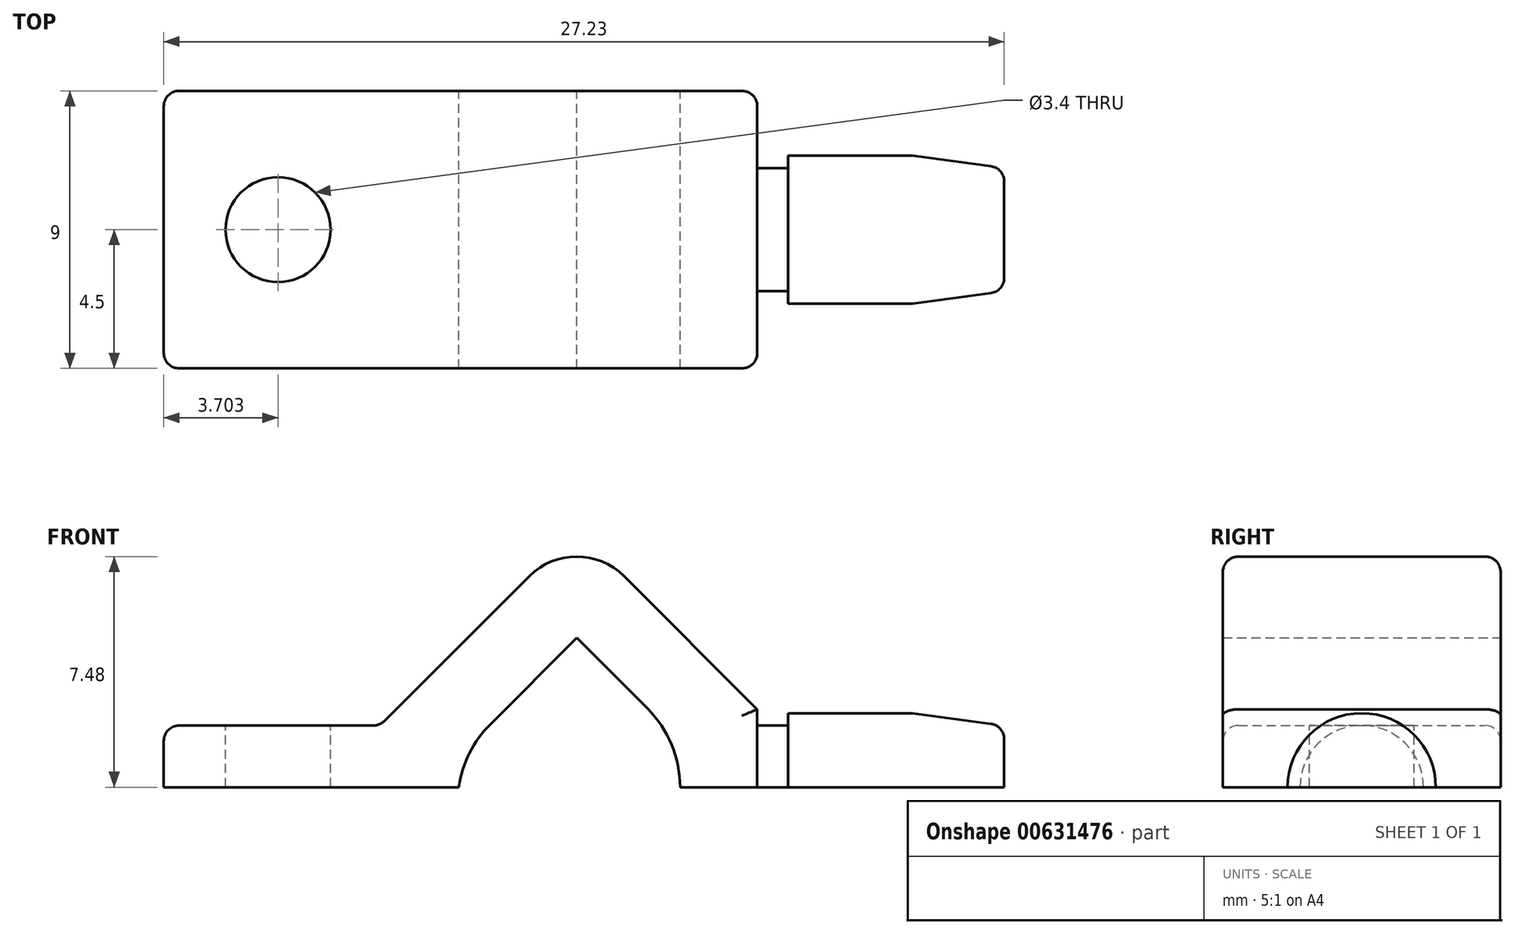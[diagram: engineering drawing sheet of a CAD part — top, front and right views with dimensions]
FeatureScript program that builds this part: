
annotation { "Feature Type Name" : "Feature", "Feature Type Description" : "" }
export const myFeature = defineFeature(function(context is Context, id is Id, definition is map)
    precondition{}
    {
        {
            var Q0;
            Q0=qCreatedBy(makeId("Front.planeOp"),FACE);
            var sketch = newSketch(context, id + "F0", { "sketchPlane" : qUnion([Q0])});
            skArc(sketch, "E0", {"start": v(-2.55, 2.05) * mm, "mid": v(-3.22, 1.1) * mm, "end": v(-3.57, 0) * mm});
            skLineSegment(sketch, "E1", {"start": v(0.25, 4.84) * mm, "end": v(2.55, 2.55) * mm});
            skLineSegment(sketch, "E2", {"start": v(0.25, 4.84) * mm, "end": v(-2.55, 2.05) * mm});
            skLineSegment(sketch, "E3", {"start": v(-13.13, 0) * mm, "end": v(-3.57, 0) * mm});
            skLineSegment(sketch, "E4", {"start": v(3.6, 0) * mm, "end": v(6.1, 0) * mm});
            skArc(sketch, "E5.trimOffspring", {"start": v(3.6, 0) * mm, "mid": v(3.33, 1.38) * mm, "end": v(2.55, 2.55) * mm});
            skLineSegment(sketch, "E6", {"start": v(-1.29, 6.84) * mm, "end": v(-6.13, 2) * mm});
            skLineSegment(sketch, "E7", {"start": v(-6.13, 2) * mm, "end": v(-13.13, 2) * mm});
            skLineSegment(sketch, "E8", {"start": v(-13.13, 2) * mm, "end": v(-13.13, 0) * mm});
            skLineSegment(sketch, "E9", {"start": v(-1.29, 6.84) * mm, "end": v(-1.29, 6.84) * mm});
            skLineSegment(sketch, "E10", {"start": v(1.79, 6.84) * mm, "end": v(6.1, 2.53) * mm});
            skLineSegment(sketch, "E11", {"start": v(6.1, 2.53) * mm, "end": v(6.1, 0) * mm});
            skLineSegment(sketch, "E12.trimOffspring", {"start": v(1.79, 6.84) * mm, "end": v(1.79, 6.84) * mm});
            skArc(sketch, "E13.trimOffspring", {"start": v(1.79, 6.84) * mm, "mid": v(0.25, 7.48) * mm, "end": v(-1.29, 6.84) * mm});
            skSolve(sketch);
        }
        {
            var Q0;
            Q0 = qSketchRegion(id + "F0", true);
            extrude(context, id + "F1", {"entities" : qUnion([Q0]), "endBound" : BoundingType.SYMMETRIC, "depth" : 9 * mm, "offsetDistance" : 25 * mm});
        }
        {
            var Q0;
            Q0=makeQuery(id+"F1.opExtrude","SWEPT_FACE",FACE,{"disambiguationData":[OSD([sQuery(id+"F0.wireOp",EDGE,"E11")])]});
            var sketch = newSketch(context, id + "F2", { "sketchPlane" : qUnion([Q0])});
            skArc(sketch, "E14", {"start": v(2, 0) * mm, "mid": v(0, 2) * mm, "end": v(-2, 0) * mm});
            skLineSegment(sketch, "E15", {"start": v(-2, 0) * mm, "end": v(2, 0) * mm});
            skSolve(sketch);
        }
        {
            var Q0;
            Q0 = qSketchRegion(id + "F2", true);
            extrude(context, id + "F3", {"entities" : qUnion([Q0]), "operationType" : NewBodyOperationType.ADD, "depth" : 1 * mm, "offsetDistance" : 25 * mm});
        }
        {
            var Q0;
            Q0=makeQuery(id+"F3.opExtrude","CAP_FACE",FACE,{"disambiguationData":[OSD([sQuery(id+"F2.wireOp",EDGE,"E14"),sQuery(id+"F2.wireOp",EDGE,"E15")])],"isStart":false});
            var sketch = newSketch(context, id + "F4", { "sketchPlane" : qUnion([Q0])});
            skArc(sketch, "E16", {"start": v(2.4, 0) * mm, "mid": v(0, 2.4) * mm, "end": v(-2.4, 0) * mm});
            skLineSegment(sketch, "E17", {"start": v(-2.4, 0) * mm, "end": v(2.4, 0) * mm});
            skSolve(sketch);
        }
        {
            var Q0;
            Q0 = qSketchRegion(id + "F4", true);
            extrude(context, id + "F5", {"entities" : qUnion([Q0]), "operationType" : NewBodyOperationType.ADD, "depth" : 7 * mm, "offsetDistance" : 25 * mm});
        }
        {
            var Q0;
            Q0=makeQuery(id+"F1.opExtrude","SWEPT_FACE",FACE,{"disambiguationData":[OSD([sQuery(id+"F0.wireOp",EDGE,"E7")])]});
            var sketch = newSketch(context, id + "F6", { "sketchPlane" : qUnion([Q0])});
            skCircle(sketch, "E18", {"center": v(-9.43, 0) * mm, "radius": 1.7 * mm});
            skSolve(sketch);
        }
        {
            var Q0;
            Q0 = qSketchRegion(id + "F6", true);
            extrude(context, id + "F7", {"entities" : qUnion([Q0]), "operationType" : NewBodyOperationType.REMOVE, "endBound" : BoundingType.THROUGH_ALL, "oppositeDirection" : true, "depth" : 25 * mm, "offsetDistance" : 25 * mm});
        }
        {
            var Q0;
            Q0=makeQuery(id+"F5.opExtrude","CAP_EDGE",EDGE,{"disambiguationData":[OSD([sQuery(id+"F4.wireOp",EDGE,"E16")])],"isStart":false});
            chamfer(context, id + "F8", {"entities" : qUnion([Q0]), "chamferType" : ChamferType.TWO_OFFSETS, "width1" : 0.4 * mm, "oppositeDirection" : false, "width2" : 3 * mm, "tangentPropagation" : true});
        }
        {
            var Q0;
            Q0=makeQuery(id+"F3.opExtrude","CAP_EDGE",EDGE,{"disambiguationData":[OSD([sQuery(id+"F2.wireOp",EDGE,"E14")])],"isStart":true});
            var Q1;
            Q1=makeQuery(id+"F3.opExtrude","CAP_EDGE",EDGE,{"disambiguationData":[OSD([sQuery(id+"F2.wireOp",EDGE,"E14")])],"isStart":false});
            var Q2;
            Q2=makeQuery(id+"F1.opExtrude","CAP_EDGE",EDGE,{"disambiguationData":[OSD([sQuery(id+"F0.wireOp",EDGE,"E10")])],"isStart":false});
            var Q3;
            Q3=makeQuery(id+"F1.opExtrude","CAP_EDGE",EDGE,{"disambiguationData":[OSD([sQuery(id+"F0.wireOp",EDGE,"E8")])],"isStart":false});
            var Q4;
            Q4=makeQuery(id+"F1.opExtrude","CAP_EDGE",EDGE,{"disambiguationData":[OSD([sQuery(id+"F0.wireOp",EDGE,"E8")])],"isStart":true});
            var Q5;
            Q5=makeQuery(id+"F1.opExtrude","CAP_EDGE",EDGE,{"disambiguationData":[OSD([sQuery(id+"F0.wireOp",EDGE,"E7")])],"isStart":true});
            var Q6;
            Q6=makeQuery(id+"F1.opExtrude","SWEPT_EDGE",EDGE,{"disambiguationData":[OSD([sQuery(id+"F0.wireOp",EDGE,"E7"),sQuery(id+"F0.wireOp",EDGE,"E8")])]});
            var Q7;
            Q7=makeQuery(id+"F1.opExtrude","CAP_EDGE",EDGE,{"disambiguationData":[OSD([sQuery(id+"F0.wireOp",EDGE,"E7")])],"isStart":false});
            var Q8;
            Q8=makeQuery(id+"F1.opExtrude","CAP_EDGE",EDGE,{"disambiguationData":[OSD([sQuery(id+"F0.wireOp",EDGE,"E6")])],"isStart":true});
            var Q9;
            Q9=makeQuery(id+"F1.opExtrude","CAP_EDGE",EDGE,{"disambiguationData":[OSD([sQuery(id+"F0.wireOp",EDGE,"E11")])],"isStart":true});
            var Q10;
            Q10=makeQuery(id+"F1.opExtrude","CAP_EDGE",EDGE,{"disambiguationData":[OSD([sQuery(id+"F0.wireOp",EDGE,"E11")])],"isStart":false});
            var Q11;
            Q11=makeQuery(id+"F1.opExtrude","SWEPT_EDGE",EDGE,{"disambiguationData":[OSD([sQuery(id+"F0.wireOp",EDGE,"E6"),sQuery(id+"F0.wireOp",EDGE,"E7")])]});
            var Q12;
            {var subQ0=sQuery(id+"F4.wireOp",EDGE,"E16");Q12=makeQuery(id+"F8.opChamfer","BLEND_EDGE",EDGE,{"blendedFrom":[makeQuery(id+"F5.opExtrude","CAP_EDGE",EDGE,{"disambiguationData":[OSD([subQ0])],"isStart":false}),makeQuery(id+"F5.opExtrude","CAP_FACE",FACE,{"disambiguationData":[OSD([subQ0,sQuery(id+"F4.wireOp",EDGE,"E17")])],"isStart":false})],"blendedInto":[makeQuery(id+"F5.opExtrude","CAP_FACE",FACE,{"disambiguationData":[OSD([subQ0,sQuery(id+"F4.wireOp",EDGE,"E17")])],"isStart":false})]});}
            var Q13;
            {var subQ0=sQuery(id+"F4.wireOp",EDGE,"E16");Q13=makeQuery(id+"F8.opChamfer","BLEND_EDGE",EDGE,{"blendedFrom":[makeQuery(id+"F5.opExtrude","CAP_EDGE",EDGE,{"disambiguationData":[OSD([subQ0])],"isStart":false}),makeQuery(id+"F5.opExtrude","SWEPT_FACE",FACE,{"disambiguationData":[OSD([subQ0])]})],"blendedInto":[makeQuery(id+"F5.opExtrude","SWEPT_FACE",FACE,{"disambiguationData":[OSD([subQ0])]})]});}
            fillet(context, id + "F9", {"entities" : qUnion([Q0, Q1, Q2, Q3, Q4, Q5, Q6, Q7, Q8, Q9, Q10, Q11, Q12, Q13]), "radius" : 0.5 * mm, "tangentPropagation" : true, "allowEdgeOverflow" : false});
        }
    });
